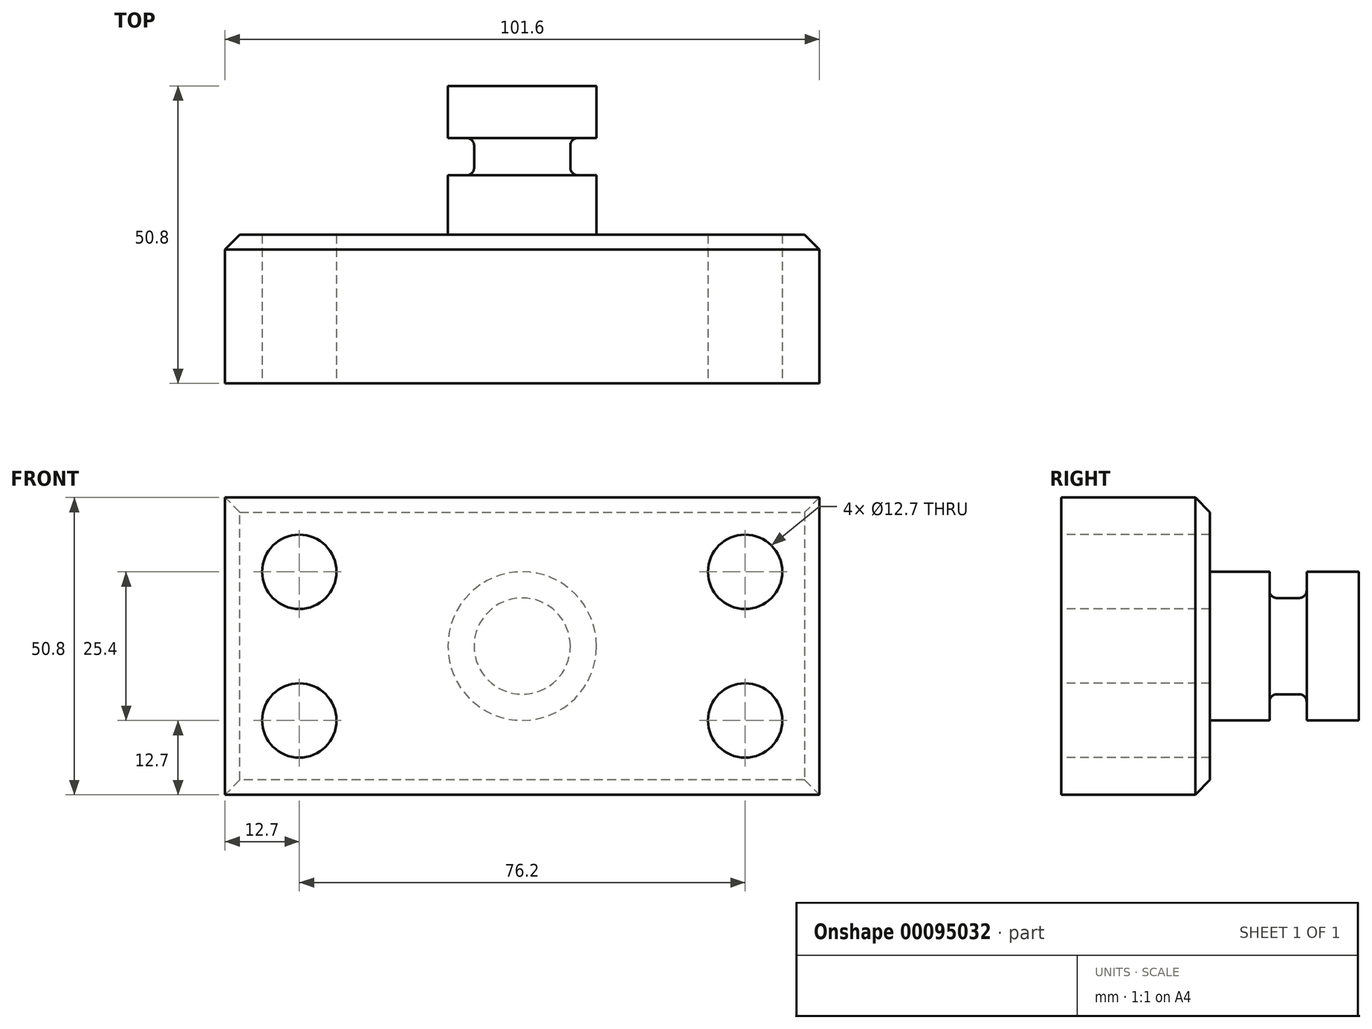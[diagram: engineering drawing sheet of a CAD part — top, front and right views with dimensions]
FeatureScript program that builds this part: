
annotation { "Feature Type Name" : "Feature", "Feature Type Description" : "" }
export const myFeature = defineFeature(function(context is Context, id is Id, definition is map)
    precondition{}
    {
        {
            var Q0;
            Q0=qCreatedBy(makeId("Front.planeOp"),FACE);
            var sketch = newSketch(context, id + "F0", { "sketchPlane" : qUnion([Q0])});
            skLineSegment(sketch, "E0.bottom", {"start": v(50.8, 25.4) * mm, "end": v(-50.8, 25.4) * mm});
            skLineSegment(sketch, "E0.top", {"start": v(50.8, -25.4) * mm, "end": v(-50.8, -25.4) * mm});
            skLineSegment(sketch, "E0.left", {"start": v(50.8, 25.4) * mm, "end": v(50.8, -25.4) * mm});
            skLineSegment(sketch, "E0.right", {"start": v(-50.8, 25.4) * mm, "end": v(-50.8, -25.4) * mm});
            skPoint(sketch, "E0.middle", {"position": v(0, 0) * mm});
            skSolve(sketch);
        }
        {
            var Q0;
            Q0 = qSketchRegion(id + "F0", true);
            extrude(context, id + "F1", {"entities" : qUnion([Q0]), "depth" : 25.4 * mm});
        }
        {
            var Q0;
            Q0=makeQuery(id+"F1.opExtrude","CAP_FACE",FACE,{"disambiguationData":[OSD([sQuery(id+"F0.wireOp",EDGE,"E0.bottom"),sQuery(id+"F0.wireOp",EDGE,"E0.top"),sQuery(id+"F0.wireOp",EDGE,"E0.left"),sQuery(id+"F0.wireOp",EDGE,"E0.right")])],"isStart":false});
            var sketch = newSketch(context, id + "F2", { "sketchPlane" : qUnion([Q0])});
            skCircle(sketch, "E1", {"center": v(-38.1, 12.7) * mm, "radius": 6.35 * mm});
            skCircle(sketch, "E2", {"center": v(-38.1, -12.7) * mm, "radius": 6.35 * mm});
            skCircle(sketch, "E3", {"center": v(38.1, 12.7) * mm, "radius": 6.35 * mm});
            skCircle(sketch, "E4", {"center": v(38.1, -12.7) * mm, "radius": 6.35 * mm});
            skSolve(sketch);
        }
        {
            var Q0;
            Q0=makeQuery(id+"F2.imprint","IMPRINT",FACE,{"disambiguationData":[TD([[makeQuery(id+"F2.imprint","IMPRINT",EDGE,{"derivedFrom":sQuery(id+"F2.wireOp",EDGE,"E1")}),1.0]])]});
            var Q1;
            Q1=makeQuery(id+"F2.imprint","IMPRINT",FACE,{"disambiguationData":[TD([[makeQuery(id+"F2.imprint","IMPRINT",EDGE,{"derivedFrom":sQuery(id+"F2.wireOp",EDGE,"E2")}),1.0]])]});
            var Q2;
            Q2=makeQuery(id+"F2.imprint","IMPRINT",FACE,{"disambiguationData":[TD([[makeQuery(id+"F2.imprint","IMPRINT",EDGE,{"derivedFrom":sQuery(id+"F2.wireOp",EDGE,"E4")}),1.0]])]});
            var Q3;
            Q3=makeQuery(id+"F2.imprint","IMPRINT",FACE,{"disambiguationData":[TD([[makeQuery(id+"F2.imprint","IMPRINT",EDGE,{"derivedFrom":sQuery(id+"F2.wireOp",EDGE,"E3")}),1.0]])]});
            extrude(context, id + "F3", {"entities" : qUnion([Q0, Q1, Q2, Q3]), "operationType" : NewBodyOperationType.REMOVE, "endBound" : BoundingType.THROUGH_ALL, "oppositeDirection" : true, "depth" : 25.4 * mm});
        }
        {
            var Q0;
            Q0=qCreatedBy(makeId("Top.planeOp"),FACE);
            var sketch = newSketch(context, id + "F4", { "sketchPlane" : qUnion([Q0])});
            skLineSegment(sketch, "E5.bottom", {"start": v(-12.7, 0) * mm, "end": v(0, 0) * mm});
            skLineSegment(sketch, "E5.top", {"start": v(-12.7, 25.4) * mm, "end": v(0, 25.4) * mm});
            skLineSegment(sketch, "E5.left", {"start": v(-12.7, 0) * mm, "end": v(-12.7, 25.4) * mm});
            skLineSegment(sketch, "E5.right", {"start": v(0, 0) * mm, "end": v(0, 25.4) * mm});
            skSolve(sketch);
        }
        {
            var Q0;
            Q0 = qSketchRegion(id + "F4", true);
            var Q1;
            Q1=sQuery(id+"F4.wireOp",EDGE,"E5.right");
            revolve(context, id + "F5", {"operationType" : NewBodyOperationType.ADD, "entities" : qUnion([Q0]), "axis" : qUnion([Q1]), "revolveType" : RevolveType.FULL});
        }
        {
            var Q0;
            Q0=qCreatedBy(makeId("Top.planeOp"),FACE);
            var sketch = newSketch(context, id + "F6", { "sketchPlane" : qUnion([Q0])});
            skLineSegment(sketch, "E6.bottom", {"start": v(-18.38, 16.5) * mm, "end": v(-8.22, 16.5) * mm});
            skLineSegment(sketch, "E6.top", {"start": v(-18.38, 10.16) * mm, "end": v(-8.22, 10.16) * mm});
            skLineSegment(sketch, "E6.left", {"start": v(-18.38, 16.5) * mm, "end": v(-18.38, 10.16) * mm});
            skLineSegment(sketch, "E6.right", {"start": v(-8.22, 16.5) * mm, "end": v(-8.22, 10.16) * mm});
            skLineSegment(sketch, "E7", {"start": v(0, 0) * mm, "end": v(0, 25.88) * mm, "construction": true});
            skSolve(sketch);
        }
        {
            var Q0;
            Q0 = qSketchRegion(id + "F6", true);
            var Q1;
            Q1=sQuery(id+"F6.wireOp",EDGE,"E7");
            revolve(context, id + "F7", {"operationType" : NewBodyOperationType.REMOVE, "entities" : qUnion([Q0]), "axis" : qUnion([Q1]), "revolveType" : RevolveType.FULL, "oppositeDirection" : true});
        }
        {
            var Q0;
            Q0=makeQuery(id+"F5.opRevolve","SWEPT_EDGE",EDGE,{"disambiguationData":[OSD([sQuery(id+"F4.wireOp",EDGE,"E5.bottom"),sQuery(id+"F4.wireOp",EDGE,"E5.left")])]});
            var Q1;
            Q1=makeQuery(id+"F7.boolean.opBoolean","COPY",EDGE,{"derivedFrom":makeQuery(id+"F7.opRevolve","SWEPT_EDGE",EDGE,{"disambiguationData":[OSD([sQuery(id+"F6.wireOp",EDGE,"E6.top"),sQuery(id+"F6.wireOp",EDGE,"E6.right")])]})});
            var Q2;
            Q2=makeQuery(id+"F7.boolean.opBoolean","COPY",EDGE,{"derivedFrom":makeQuery(id+"F7.opRevolve","SWEPT_EDGE",EDGE,{"disambiguationData":[OSD([sQuery(id+"F6.wireOp",EDGE,"E6.bottom"),sQuery(id+"F6.wireOp",EDGE,"E6.right")])]})});
            fillet(context, id + "F8", {"entities" : qUnion([Q0, Q1, Q2]), "radius" : 1.27 * mm, "tangentPropagation" : true, "allowEdgeOverflow" : false});
        }
        {
            var Q0;
            Q0=makeQuery(id+"F1.opExtrude","CAP_EDGE",EDGE,{"disambiguationData":[OSD([sQuery(id+"F0.wireOp",EDGE,"E0.top")])],"isStart":true});
            var Q1;
            Q1=makeQuery(id+"F1.opExtrude","CAP_EDGE",EDGE,{"disambiguationData":[OSD([sQuery(id+"F0.wireOp",EDGE,"E0.right")])],"isStart":true});
            var Q2;
            Q2=makeQuery(id+"F1.opExtrude","CAP_EDGE",EDGE,{"disambiguationData":[OSD([sQuery(id+"F0.wireOp",EDGE,"E0.bottom")])],"isStart":true});
            var Q3;
            Q3=makeQuery(id+"F1.opExtrude","CAP_EDGE",EDGE,{"disambiguationData":[OSD([sQuery(id+"F0.wireOp",EDGE,"E0.left")])],"isStart":true});
            chamfer(context, id + "F9", {"entities" : qUnion([Q0, Q1, Q2, Q3]), "width" : 2.54 * mm, "tangentPropagation" : true});
        }
    });
